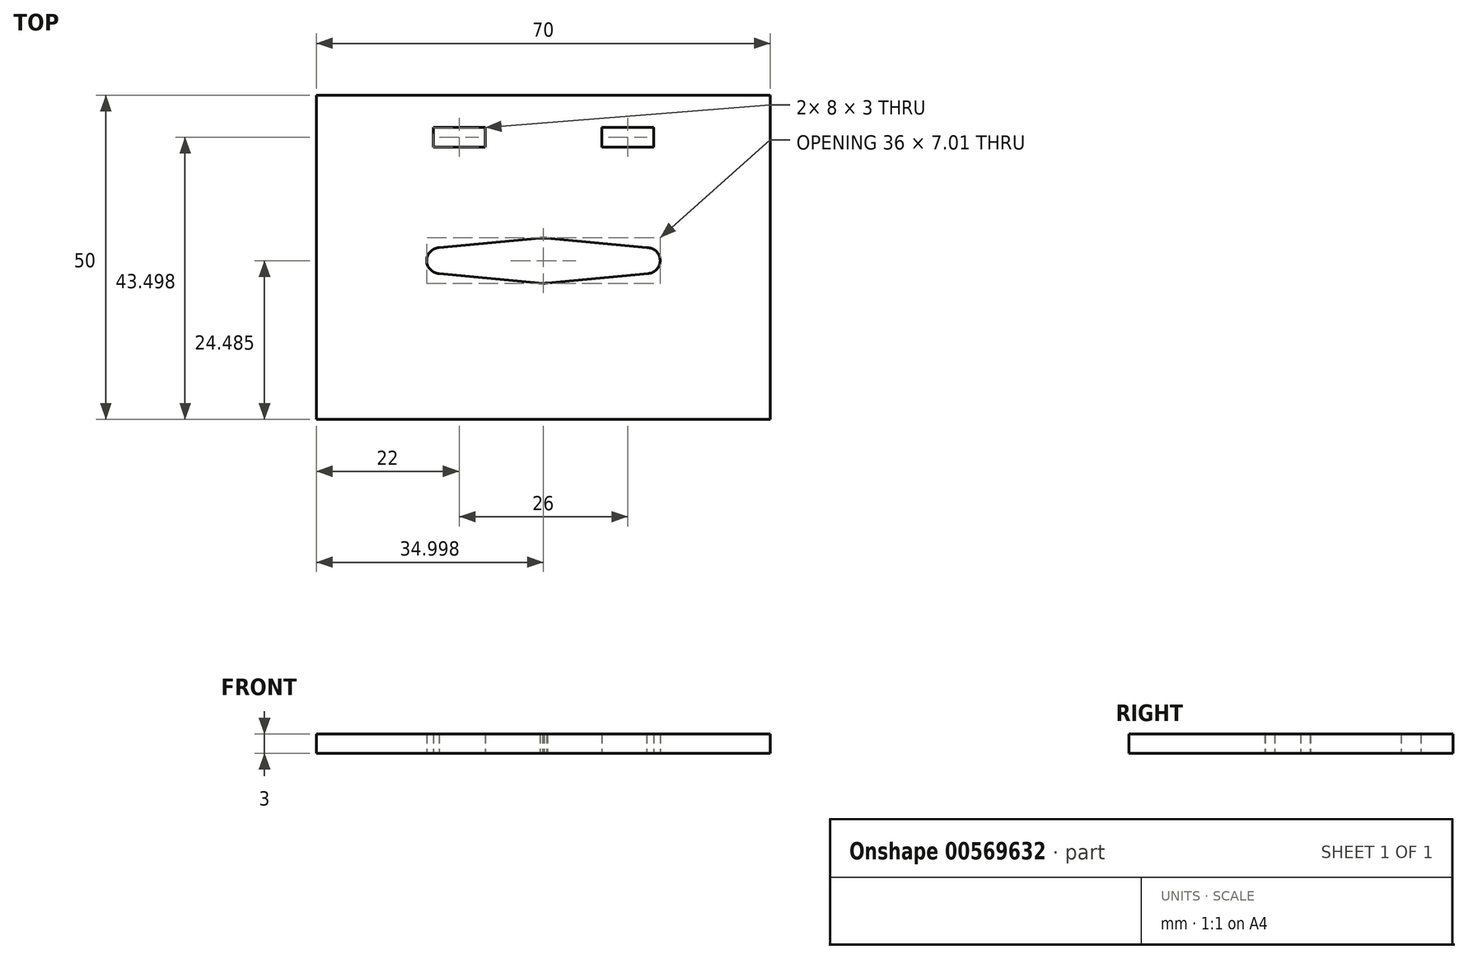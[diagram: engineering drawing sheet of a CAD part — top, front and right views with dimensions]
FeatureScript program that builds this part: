
annotation { "Feature Type Name" : "Feature", "Feature Type Description" : "" }
export const myFeature = defineFeature(function(context is Context, id is Id, definition is map)
    precondition{}
    {
        {
            var Q0;
            Q0=qCreatedBy(makeId("Top.planeOp"),FACE);
            var sketch = newSketch(context, id + "F0", { "sketchPlane" : qUnion([Q0])});
            skLineSegment(sketch, "E0.bottom", {"start": v(-35, 25.52) * mm, "end": v(35, 25.52) * mm});
            skLineSegment(sketch, "E0.top", {"start": v(-35, -24.48) * mm, "end": v(35, -24.48) * mm});
            skLineSegment(sketch, "E0.left", {"start": v(-35, 25.52) * mm, "end": v(-35, -24.48) * mm});
            skLineSegment(sketch, "E0.right", {"start": v(35, 25.52) * mm, "end": v(35, -24.48) * mm});
            skLineSegment(sketch, "E1", {"start": v(-48.5, 20.52) * mm, "end": v(41.04, 20.52) * mm, "construction": true});
            skLineSegment(sketch, "E2", {"start": v(-48.5, 17.52) * mm, "end": v(44.02, 17.52) * mm, "construction": true});
            skLineSegment(sketch, "E3", {"start": v(9, 20.52) * mm, "end": v(9, 17.52) * mm});
            skLineSegment(sketch, "E4", {"start": v(9, 17.52) * mm, "end": v(17, 17.52) * mm});
            skLineSegment(sketch, "E5", {"start": v(17, 17.52) * mm, "end": v(17, 20.52) * mm});
            skLineSegment(sketch, "E6", {"start": v(17, 20.52) * mm, "end": v(9, 20.52) * mm});
            skLineSegment(sketch, "E7.MirrorCS", {"start": v(-9, 20.52) * mm, "end": v(-9, 17.52) * mm});
            skLineSegment(sketch, "E8.MirrorCS", {"start": v(-17, 17.52) * mm, "end": v(-17, 20.52) * mm});
            skLineSegment(sketch, "E9", {"start": v(-17, 20.52) * mm, "end": v(-9, 20.52) * mm});
            skLineSegment(sketch, "E10", {"start": v(-17, 17.52) * mm, "end": v(-9, 17.52) * mm});
            skArc(sketch, "E11", {"start": v(0, -3.5) * mm, "mid": v(0.32, -3.48) * mm, "end": v(0.65, -3.44) * mm});
            skArc(sketch, "E12", {"start": v(-16.06, 2) * mm, "mid": v(-18, 0) * mm, "end": v(-16.07, -2) * mm});
            skArc(sketch, "E13.MirrorC", {"start": v(15.95, 2) * mm, "mid": v(18, 0.12) * mm, "end": v(16.19, -2) * mm});
            skLineSegment(sketch, "E14", {"start": v(0, -3.5) * mm, "end": v(16.19, -2) * mm});
            skLineSegment(sketch, "E15", {"start": v(0, 3.51) * mm, "end": v(-0.51, 3.46) * mm});
            skLineSegment(sketch, "E16", {"start": v(0, -3.5) * mm, "end": v(-16.07, -2) * mm});
            skLineSegment(sketch, "E17", {"start": v(0, 3.51) * mm, "end": v(15.95, 2) * mm});
            skLineSegment(sketch, "E18", {"start": v(-16.06, 2) * mm, "end": v(-0.51, 3.46) * mm});
            skArc(sketch, "E19.trimOffspring", {"start": v(0.52, 3.46) * mm, "mid": v(0, 3.5) * mm, "end": v(-0.51, 3.46) * mm});
            skSolve(sketch);
        }
        {
            var Q0;
            Q0 = qSketchRegion(id + "F0", true);
            extrude(context, id + "F1", {"entities" : qUnion([Q0]), "depth" : 3 * mm, "offsetDistance" : 25 * mm});
        }
    });
